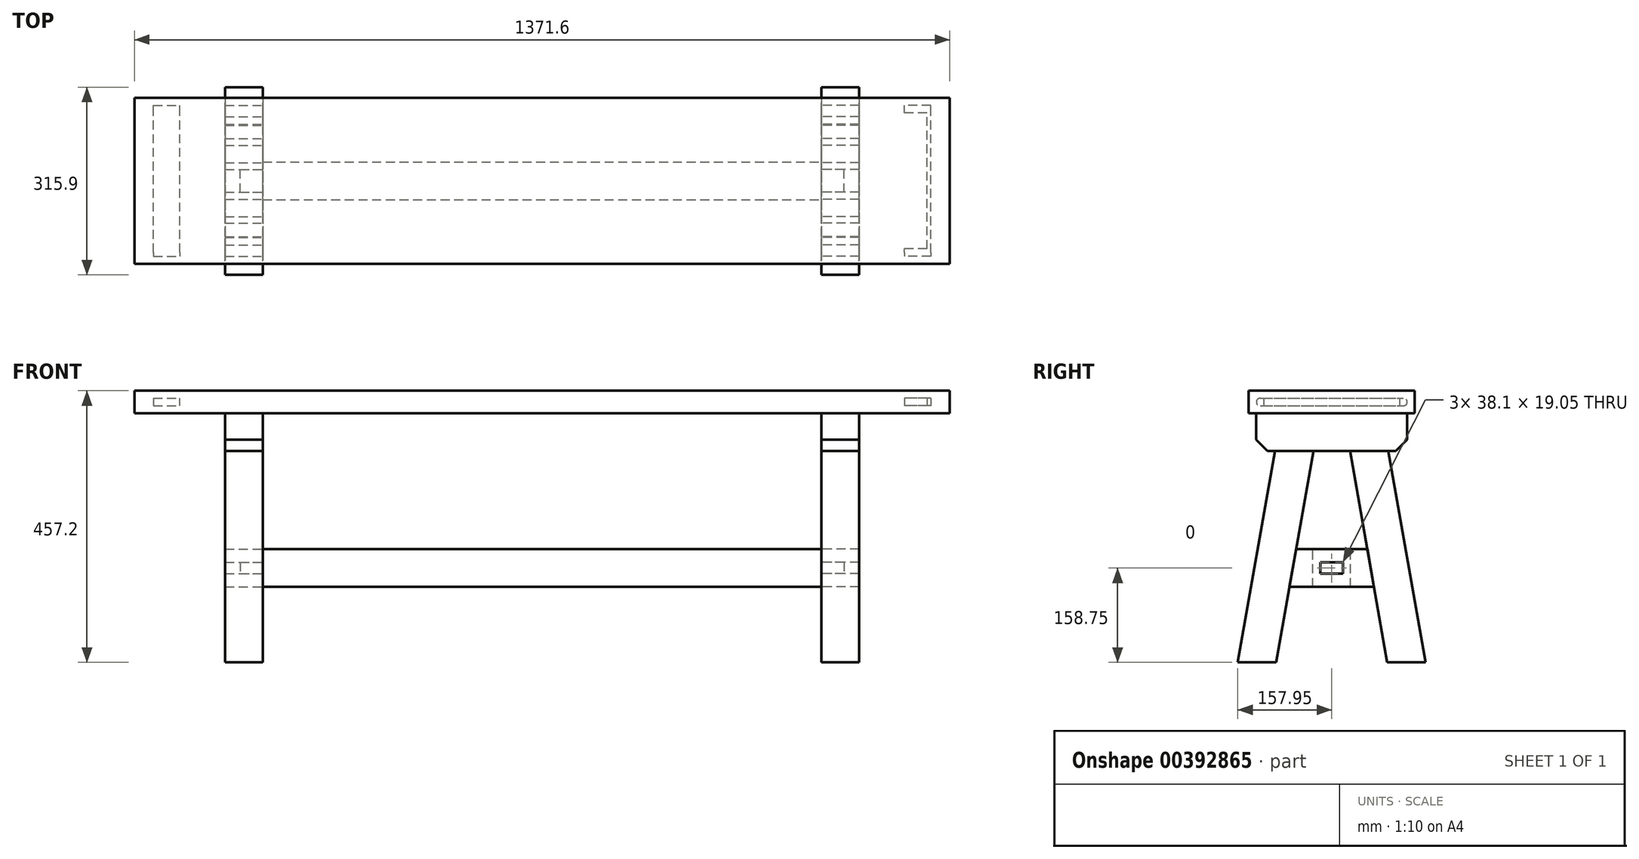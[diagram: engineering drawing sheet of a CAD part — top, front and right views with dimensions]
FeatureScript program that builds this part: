
annotation { "Feature Type Name" : "Feature", "Feature Type Description" : "" }
export const myFeature = defineFeature(function(context is Context, id is Id, definition is map)
    precondition{}
    {
        {
            var Q0;
            Q0=qCreatedBy(makeId("Right.planeOp"),FACE);
            var sketch = newSketch(context, id + "F0", { "sketchPlane" : qUnion([Q0])});
            skLineSegment(sketch, "E0.bottom", {"start": v(-139.7, 457.2) * mm, "end": v(139.7, 457.2) * mm});
            skLineSegment(sketch, "E0.top", {"start": v(-139.7, 419.1) * mm, "end": v(139.7, 419.1) * mm});
            skLineSegment(sketch, "E0.left", {"start": v(-139.7, 457.2) * mm, "end": v(-139.7, 419.1) * mm});
            skLineSegment(sketch, "E0.right", {"start": v(139.7, 457.2) * mm, "end": v(139.7, 419.1) * mm});
            skLineSegment(sketch, "E1", {"start": v(0, 0) * mm, "end": v(0, 419.1) * mm, "construction": true});
            skSolve(sketch);
        }
        {
            var Q0;
            Q0 = qSketchRegion(id + "F0", true);
            extrude(context, id + "F1", {"entities" : qUnion([Q0]), "endBound" : BoundingType.SYMMETRIC, "depth" : 1219.2 * mm});
        }
        {
            var Q0;
            Q0=makeQuery(id+"F1.opExtrude","CAP_FACE",FACE,{"disambiguationData":[OSD([sQuery(id+"F0.wireOp",EDGE,"E0.bottom"),sQuery(id+"F0.wireOp",EDGE,"E0.top"),sQuery(id+"F0.wireOp",EDGE,"E0.left"),sQuery(id+"F0.wireOp",EDGE,"E0.right")])],"isStart":false});
            var sketch = newSketch(context, id + "F2", { "sketchPlane" : qUnion([Q0])});
            skPoint(sketch, "E2.firstSnap0", {"position": v(-139.7, 438.15) * mm});
            skLineSegment(sketch, "E2.bottom", {"start": v(-114.3, 444.5) * mm, "end": v(114.3, 444.5) * mm});
            skLineSegment(sketch, "E2.top", {"start": v(-114.3, 431.8) * mm, "end": v(114.3, 431.8) * mm});
            skLineSegment(sketch, "E2.left", {"start": v(-114.3, 444.5) * mm, "end": v(-114.3, 431.8) * mm});
            skLineSegment(sketch, "E2.right", {"start": v(114.3, 444.5) * mm, "end": v(114.3, 431.8) * mm});
            skLineSegment(sketch, "E3", {"start": v(0, 431.8) * mm, "end": v(0, 419.1) * mm, "construction": true});
            skLineSegment(sketch, "E4", {"start": v(-114.3, 438.15) * mm, "end": v(-139.7, 438.15) * mm, "construction": true});
            skSolve(sketch);
        }
        {
            var Q0;
            Q0 = qSketchRegion(id + "F2", true);
            extrude(context, id + "F3", {"entities" : qUnion([Q0]), "operationType" : NewBodyOperationType.ADD, "depth" : 38.1 * mm});
        }
        {
            var Q0;
            Q0=makeQuery(id+"F1.opExtrude","CAP_FACE",FACE,{"disambiguationData":[OSD([sQuery(id+"F0.wireOp",EDGE,"E0.bottom"),sQuery(id+"F0.wireOp",EDGE,"E0.top"),sQuery(id+"F0.wireOp",EDGE,"E0.left"),sQuery(id+"F0.wireOp",EDGE,"E0.right")])],"isStart":false});
            var sketch = newSketch(context, id + "F4", { "sketchPlane" : qUnion([Q0])});
            skLineSegment(sketch, "E5.bottom", {"start": v(-139.7, 457.2) * mm, "end": v(139.7, 457.2) * mm});
            skLineSegment(sketch, "E5.top", {"start": v(-139.7, 419.1) * mm, "end": v(139.7, 419.1) * mm});
            skLineSegment(sketch, "E5.left", {"start": v(-139.7, 457.2) * mm, "end": v(-139.7, 419.1) * mm});
            skLineSegment(sketch, "E5.right", {"start": v(139.7, 457.2) * mm, "end": v(139.7, 419.1) * mm});
            skLineSegment(sketch, "E6.bottom", {"start": v(-120.4, 444.5) * mm, "end": v(120.65, 444.5) * mm});
            skLineSegment(sketch, "E6.top", {"start": v(-120.4, 431.8) * mm, "end": v(120.65, 431.8) * mm});
            skLineSegment(sketch, "E6.left", {"start": v(-120.4, 444.5) * mm, "end": v(-120.4, 431.8) * mm, "construction": true});
            skLineSegment(sketch, "E6.right", {"start": v(120.65, 444.5) * mm, "end": v(120.65, 431.8) * mm, "construction": true});
            skArc(sketch, "E7", {"start": v(-120.4, 444.5) * mm, "mid": v(-126.75, 438.15) * mm, "end": v(-120.4, 431.8) * mm});
            skArc(sketch, "E8", {"start": v(120.65, 431.8) * mm, "mid": v(127, 438.15) * mm, "end": v(120.65, 444.5) * mm});
            skSolve(sketch);
        }
        {
            var Q0;
            Q0 = qSketchRegion(id + "F4", true);
            extrude(context, id + "F5", {"entities" : qUnion([Q0]), "depth" : 76.2 * mm});
        }
        {
            var Q0;
            Q0=makeQuery(id+"F3.opExtrude","CAP_FACE",FACE,{"disambiguationData":[OSD([sQuery(id+"F2.wireOp",EDGE,"E2.bottom"),sQuery(id+"F2.wireOp",EDGE,"E2.top"),sQuery(id+"F2.wireOp",EDGE,"E2.left"),sQuery(id+"F2.wireOp",EDGE,"E2.right")])],"isStart":false});
            var sketch = newSketch(context, id + "F6", { "sketchPlane" : qUnion([Q0])});
            skLineSegment(sketch, "E9.0", {"start": v(-120.4, 431.8) * mm, "end": v(120.65, 431.8) * mm});
            skArc(sketch, "E9.1", {"start": v(120.65, 431.8) * mm, "mid": v(127, 438.15) * mm, "end": v(120.65, 444.5) * mm});
            skLineSegment(sketch, "E9.2", {"start": v(-120.4, 444.5) * mm, "end": v(120.65, 444.5) * mm});
            skArc(sketch, "E9.3", {"start": v(-120.4, 444.5) * mm, "mid": v(-126.75, 438.15) * mm, "end": v(-120.4, 431.8) * mm});
            skSolve(sketch);
        }
        {
            var Q0;
            Q0 = qSketchRegion(id + "F6", true);
            var Q1;
            Q1=makeQuery(id+"F5.opExtrude","CAP_FACE",FACE,{"disambiguationData":[OSD([sQuery(id+"F4.wireOp",EDGE,"E5.bottom"),sQuery(id+"F4.wireOp",EDGE,"E5.top"),sQuery(id+"F4.wireOp",EDGE,"E5.left"),sQuery(id+"F4.wireOp",EDGE,"E5.right"),sQuery(id+"F4.wireOp",EDGE,"E6.bottom"),sQuery(id+"F4.wireOp",EDGE,"E6.top"),sQuery(id+"F4.wireOp",EDGE,"E7"),sQuery(id+"F4.wireOp",EDGE,"E8")])],"isStart":false});
            extrude(context, id + "F7", {"entities" : qUnion([Q0]), "operationType" : NewBodyOperationType.ADD, "endBound" : BoundingType.UP_TO_SURFACE, "endBoundEntityFace" : qUnion([Q1]), "depth" : 25.4 * mm, "hasSecondDirection" : true, "secondDirectionOppositeDirection" : false, "secondDirectionDepth" : 6.35 * mm});
        }
        {
            var Q0;
            Q0=makeQuery(id+"F5.opExtrude","SWEPT_BODY",BODY,{"disambiguationData":[OSD([sQuery(id+"F4.wireOp",EDGE,"E5.bottom"),sQuery(id+"F4.wireOp",EDGE,"E5.top"),sQuery(id+"F4.wireOp",EDGE,"E5.left"),sQuery(id+"F4.wireOp",EDGE,"E5.right"),sQuery(id+"F4.wireOp",EDGE,"E6.bottom"),sQuery(id+"F4.wireOp",EDGE,"E6.top"),sQuery(id+"F4.wireOp",EDGE,"E7"),sQuery(id+"F4.wireOp",EDGE,"E8")])]});
            var Q1;
            Q1=qCreatedBy(makeId("Right.planeOp"),FACE);
            mirror(context, id + "F8", {"operationType" : NewBodyOperationType.ADD, "entities" : qUnion([Q0]), "mirrorPlane" : qUnion([Q1])});
        }
        {
            var Q0;
            Q0=qCreatedBy(makeId("Right.planeOp"),FACE);
            var sketch = newSketch(context, id + "F9", { "sketchPlane" : qUnion([Q0])});
            skLineSegment(sketch, "E10.bottom", {"start": v(-31.75, 127) * mm, "end": v(31.75, 127) * mm});
            skLineSegment(sketch, "E10.top", {"start": v(-31.75, 190.5) * mm, "end": v(31.75, 190.5) * mm});
            skLineSegment(sketch, "E10.left", {"start": v(-31.75, 127) * mm, "end": v(-31.75, 190.5) * mm});
            skLineSegment(sketch, "E10.right", {"start": v(31.75, 127) * mm, "end": v(31.75, 190.5) * mm});
            skLineSegment(sketch, "E11", {"start": v(0, 0) * mm, "end": v(0, 127) * mm, "construction": true});
            skSolve(sketch);
        }
        {
            var Q0;
            Q0 = qSketchRegion(id + "F9", true);
            extrude(context, id + "F10", {"entities" : qUnion([Q0]), "endBound" : BoundingType.SYMMETRIC, "oppositeDirection" : true, "depth" : 939.8 * mm});
        }
        {
            var Q0;
            Q0=makeQuery(id+"F10.opExtrude","CAP_FACE",FACE,{"disambiguationData":[OSD([sQuery(id+"F9.wireOp",EDGE,"E10.bottom"),sQuery(id+"F9.wireOp",EDGE,"E10.top"),sQuery(id+"F9.wireOp",EDGE,"E10.left"),sQuery(id+"F9.wireOp",EDGE,"E10.right")])],"isStart":true});
            var sketch = newSketch(context, id + "F11", { "sketchPlane" : qUnion([Q0])});
            skLineSegment(sketch, "E12.bottom", {"start": v(-19.05, 168.28) * mm, "end": v(19.05, 168.28) * mm});
            skLineSegment(sketch, "E12.top", {"start": v(-19.05, 149.22) * mm, "end": v(19.05, 149.22) * mm});
            skLineSegment(sketch, "E12.left", {"start": v(-19.05, 168.28) * mm, "end": v(-19.05, 149.22) * mm});
            skLineSegment(sketch, "E12.right", {"start": v(19.05, 168.28) * mm, "end": v(19.05, 149.22) * mm});
            skLineSegment(sketch, "E13", {"start": v(0, 168.28) * mm, "end": v(0, 190.5) * mm, "construction": true});
            skLineSegment(sketch, "E14", {"start": v(-19.05, 158.75) * mm, "end": v(-31.75, 158.75) * mm, "construction": true});
            skPoint(sketch, "E14.endSnap0", {"position": v(-31.75, 158.75) * mm});
            skSolve(sketch);
        }
        {
            var Q0;
            Q0=makeQuery(id+"F11.imprint","IMPRINT",FACE,{"disambiguationData":[TD([[makeQuery(id+"F11.imprint","IMPRINT",EDGE,{"derivedFrom":sQuery(id+"F11.wireOp",EDGE,"E12.bottom")}),-1.0]])]});
            var Q1;
            Q1=sQuery(id+"F11.wireOp",EDGE,"E12.bottom");
            var Q2;
            Q2=sQuery(id+"F11.wireOp",EDGE,"E12.left");
            extrude(context, id + "F12", {"entities" : qUnion([Q0]), "operationType" : NewBodyOperationType.ADD, "surfaceEntities" : qUnion([Q1, Q2]), "depth" : 38.1 * mm});
        }
        {
            var Q0;
            Q0=makeQuery(id+"F10.opExtrude","SWEPT_BODY",BODY,{"disambiguationData":[OSD([sQuery(id+"F9.wireOp",EDGE,"E10.bottom"),sQuery(id+"F9.wireOp",EDGE,"E10.top"),sQuery(id+"F9.wireOp",EDGE,"E10.left"),sQuery(id+"F9.wireOp",EDGE,"E10.right")])]});
            var Q1;
            Q1=qCreatedBy(makeId("Right.planeOp"),FACE);
            mirror(context, id + "F13", {"operationType" : NewBodyOperationType.ADD, "entities" : qUnion([Q0]), "mirrorPlane" : qUnion([Q1])});
        }
        {
            var Q0;
            Q0=makeQuery(id+"F10.opExtrude","CAP_FACE",FACE,{"disambiguationData":[OSD([sQuery(id+"F9.wireOp",EDGE,"E10.bottom"),sQuery(id+"F9.wireOp",EDGE,"E10.top"),sQuery(id+"F9.wireOp",EDGE,"E10.left"),sQuery(id+"F9.wireOp",EDGE,"E10.right")])],"isStart":true});
            var sketch = newSketch(context, id + "F14", { "sketchPlane" : qUnion([Q0])});
            skLineSegment(sketch, "E15", {"start": v(-157.95, 0) * mm, "end": v(-93.47, 0) * mm});
            skLineSegment(sketch, "E16", {"start": v(93.47, 0) * mm, "end": v(157.95, 0) * mm});
            skLineSegment(sketch, "E17", {"start": v(157.95, 0) * mm, "end": v(95.25, 355.6) * mm});
            skLineSegment(sketch, "E18", {"start": v(95.25, 355.6) * mm, "end": v(30.77, 355.6) * mm});
            skLineSegment(sketch, "E19", {"start": v(30.77, 355.6) * mm, "end": v(93.47, 0) * mm});
            skLineSegment(sketch, "E20", {"start": v(-93.47, 0) * mm, "end": v(-30.77, 355.6) * mm});
            skLineSegment(sketch, "E21", {"start": v(-30.77, 355.6) * mm, "end": v(-95.25, 355.6) * mm});
            skLineSegment(sketch, "E22", {"start": v(-95.25, 355.6) * mm, "end": v(-157.95, 0) * mm});
            skLineSegment(sketch, "E23", {"start": v(-107.95, 355.6) * mm, "end": v(107.95, 355.6) * mm});
            skLineSegment(sketch, "E24", {"start": v(107.95, 355.6) * mm, "end": v(127, 374.65) * mm});
            skLineSegment(sketch, "E25", {"start": v(127, 374.65) * mm, "end": v(127, 419.1) * mm});
            skLineSegment(sketch, "E26", {"start": v(127, 419.1) * mm, "end": v(-127, 419.1) * mm});
            skLineSegment(sketch, "E27", {"start": v(-127, 419.1) * mm, "end": v(-127, 374.65) * mm});
            skLineSegment(sketch, "E28", {"start": v(-127, 374.65) * mm, "end": v(-107.95, 355.6) * mm});
            skLineSegment(sketch, "E29", {"start": v(0, 419.1) * mm, "end": v(0, 355.6) * mm, "construction": true});
            skLineSegment(sketch, "E30", {"start": v(0, 355.6) * mm, "end": v(0, 0) * mm, "construction": true});
            skLineSegment(sketch, "E31", {"start": v(93.47, 0) * mm, "end": v(156, 11.03) * mm, "construction": true});
            skLineSegment(sketch, "E32", {"start": v(-93.47, 0) * mm, "end": v(93.47, 0) * mm, "construction": true});
            skLineSegment(sketch, "E33", {"start": v(-59.88, 190.5) * mm, "end": v(59.88, 190.5) * mm});
            skLineSegment(sketch, "E34", {"start": v(-71.08, 127) * mm, "end": v(71.08, 127) * mm});
            skLineSegment(sketch, "E35", {"start": v(157.95, 0) * mm, "end": v(95.42, -11.03) * mm, "construction": true});
            skLineSegment(sketch, "E36", {"start": v(71.08, 127) * mm, "end": v(135.56, 127) * mm, "construction": true});
            skLineSegment(sketch, "E37", {"start": v(-71.08, 127) * mm, "end": v(-135.56, 127) * mm, "construction": true});
            skLineSegment(sketch, "E38", {"start": v(-103.32, 127) * mm, "end": v(-92.12, 190.5) * mm, "construction": true});
            skLineSegment(sketch, "E39", {"start": v(-92.12, 190.5) * mm, "end": v(-59.88, 190.5) * mm, "construction": true});
            skLineSegment(sketch, "E40", {"start": v(103.32, 127) * mm, "end": v(92.12, 190.5) * mm, "construction": true});
            skLineSegment(sketch, "E41", {"start": v(92.12, 190.5) * mm, "end": v(59.88, 190.5) * mm, "construction": true});
            skLineSegment(sketch, "E42", {"start": v(-95.25, 355.6) * mm, "end": v(-89.65, 387.35) * mm, "construction": true});
            skLineSegment(sketch, "E43", {"start": v(-89.65, 387.35) * mm, "end": v(-25.17, 387.35) * mm, "construction": true});
            skLineSegment(sketch, "E44", {"start": v(-25.17, 387.35) * mm, "end": v(-30.77, 355.6) * mm, "construction": true});
            skLineSegment(sketch, "E45", {"start": v(95.25, 355.6) * mm, "end": v(89.65, 387.35) * mm, "construction": true});
            skLineSegment(sketch, "E46", {"start": v(89.65, 387.35) * mm, "end": v(25.17, 387.35) * mm, "construction": true});
            skLineSegment(sketch, "E47", {"start": v(25.17, 387.35) * mm, "end": v(30.77, 355.6) * mm, "construction": true});
            skLineSegment(sketch, "E48", {"start": v(25.17, 387.35) * mm, "end": v(19.57, 419.1) * mm, "construction": true});
            skSolve(sketch);
        }
        {
            var Q0;
            {var subQ6=sQuery(id+"F14.wireOp",EDGE,"E24");Q0=makeQuery(id+"F14.imprint","IMPRINT",FACE,{"disambiguationData":[TD([[makeQuery(id+"F14.imprint","IMPRINT",EDGE,{"derivedFrom":subQ6}),1.0]])]});}
            extrude(context, id + "F15", {"entities" : qUnion([Q0]), "depth" : 63.5 * mm});
        }
        {
            var Q0;
            {var subQ5=sQuery(id+"F14.wireOp",EDGE,"E15");Q0=makeQuery(id+"F14.imprint","IMPRINT",FACE,{"disambiguationData":[TD([[makeQuery(id+"F14.imprint","IMPRINT",EDGE,{"derivedFrom":subQ5}),1.0]])]});}
            var Q1;
            Q1=makeQuery(id+"F15.opExtrude","CAP_FACE",FACE,{"disambiguationData":[OSD([sQuery(id+"F14.wireOp",EDGE,"E23"),sQuery(id+"F14.wireOp",EDGE,"E24"),sQuery(id+"F14.wireOp",EDGE,"E25"),sQuery(id+"F14.wireOp",EDGE,"E26"),sQuery(id+"F14.wireOp",EDGE,"E27"),sQuery(id+"F14.wireOp",EDGE,"E28")])],"isStart":false});
            extrude(context, id + "F16", {"entities" : qUnion([Q0]), "endBound" : BoundingType.UP_TO_SURFACE, "endBoundEntityFace" : qUnion([Q1]), "depth" : 25.4 * mm});
        }
        {
            var Q0;
            {var subQ6=sQuery(id+"F14.wireOp",EDGE,"E16");Q0=makeQuery(id+"F14.imprint","IMPRINT",FACE,{"disambiguationData":[TD([[makeQuery(id+"F14.imprint","IMPRINT",EDGE,{"derivedFrom":subQ6}),1.0]])]});}
            var Q1;
            Q1=makeQuery(id+"F15.opExtrude","CAP_FACE",FACE,{"disambiguationData":[OSD([sQuery(id+"F14.wireOp",EDGE,"E23"),sQuery(id+"F14.wireOp",EDGE,"E24"),sQuery(id+"F14.wireOp",EDGE,"E25"),sQuery(id+"F14.wireOp",EDGE,"E26"),sQuery(id+"F14.wireOp",EDGE,"E27"),sQuery(id+"F14.wireOp",EDGE,"E28")])],"isStart":false});
            extrude(context, id + "F17", {"entities" : qUnion([Q0]), "endBound" : BoundingType.UP_TO_SURFACE, "endBoundEntityFace" : qUnion([Q1]), "depth" : 25.4 * mm});
        }
        {
            var Q0;
            {var subQ5=makeQuery(id+"F10.opExtrude","CAP_EDGE",EDGE,{"disambiguationData":[OSD([sQuery(id+"F9.wireOp",EDGE,"E10.left")])],"isStart":true});Q0=makeQuery(id+"F14.imprint","IMPRINT",FACE,{"disambiguationData":[TD([[makeQuery(id+"F14.imprint","IMPRINT",EDGE,{"derivedFrom":subQ5}),1.0]])]});}
            var Q1;
            {var subQ2=makeQuery(id+"F10.opExtrude","CAP_EDGE",EDGE,{"disambiguationData":[OSD([sQuery(id+"F9.wireOp",EDGE,"E10.left")])],"isStart":true});Q1=makeQuery(id+"F14.imprint","IMPRINT",FACE,{"disambiguationData":[TD([[makeQuery(id+"F14.imprint","IMPRINT",EDGE,{"derivedFrom":subQ2}),-1.0]])]});}
            var Q2;
            {var subQ5=makeQuery(id+"F10.opExtrude","CAP_EDGE",EDGE,{"disambiguationData":[OSD([sQuery(id+"F9.wireOp",EDGE,"E10.right")])],"isStart":true});Q2=makeQuery(id+"F14.imprint","IMPRINT",FACE,{"disambiguationData":[TD([[makeQuery(id+"F14.imprint","IMPRINT",EDGE,{"derivedFrom":subQ5}),-1.0]])]});}
            var Q3;
            Q3=makeQuery(id+"F15.opExtrude","CAP_FACE",FACE,{"disambiguationData":[OSD([sQuery(id+"F14.wireOp",EDGE,"E23"),sQuery(id+"F14.wireOp",EDGE,"E24"),sQuery(id+"F14.wireOp",EDGE,"E25"),sQuery(id+"F14.wireOp",EDGE,"E26"),sQuery(id+"F14.wireOp",EDGE,"E27"),sQuery(id+"F14.wireOp",EDGE,"E28")])],"isStart":false});
            extrude(context, id + "F18", {"entities" : qUnion([Q0, Q1, Q2]), "endBound" : BoundingType.UP_TO_SURFACE, "endBoundEntityFace" : qUnion([Q3]), "depth" : 25.4 * mm});
        }
        {
            var Q0;
            Q0=makeQuery(id+"F16.opExtrude","SWEPT_BODY",BODY,{"disambiguationData":[OSD([sQuery(id+"F14.wireOp",EDGE,"E15"),sQuery(id+"F14.wireOp",EDGE,"E20"),sQuery(id+"F14.wireOp",EDGE,"E22"),sQuery(id+"F14.wireOp",EDGE,"E23")])]});
            var Q1;
            Q1=makeQuery(id+"F15.opExtrude","SWEPT_BODY",BODY,{"disambiguationData":[OSD([sQuery(id+"F14.wireOp",EDGE,"E23"),sQuery(id+"F14.wireOp",EDGE,"E24"),sQuery(id+"F14.wireOp",EDGE,"E25"),sQuery(id+"F14.wireOp",EDGE,"E26"),sQuery(id+"F14.wireOp",EDGE,"E27"),sQuery(id+"F14.wireOp",EDGE,"E28")])]});
            var Q2;
            Q2=makeQuery(id+"F17.opExtrude","SWEPT_BODY",BODY,{"disambiguationData":[OSD([sQuery(id+"F14.wireOp",EDGE,"E16"),sQuery(id+"F14.wireOp",EDGE,"E17"),sQuery(id+"F14.wireOp",EDGE,"E19"),sQuery(id+"F14.wireOp",EDGE,"E23")])]});
            var Q3;
            Q3=makeQuery(id+"F18.opExtrude","SWEPT_BODY",BODY,{"disambiguationData":[OSD([sQuery(id+"F11.wireOp",EDGE,"E12.bottom"),sQuery(id+"F11.wireOp",EDGE,"E12.top"),sQuery(id+"F11.wireOp",EDGE,"E12.left"),sQuery(id+"F11.wireOp",EDGE,"E12.right"),sQuery(id+"F14.wireOp",EDGE,"E19"),sQuery(id+"F14.wireOp",EDGE,"E20"),sQuery(id+"F14.wireOp",EDGE,"E33"),sQuery(id+"F14.wireOp",EDGE,"E34")])]});
            var Q4;
            Q4=qCreatedBy(makeId("Right.planeOp"),FACE);
            mirror(context, id + "F19", {"entities" : qUnion([Q0, Q1, Q2, Q3]), "mirrorPlane" : qUnion([Q4])});
        }
    });
